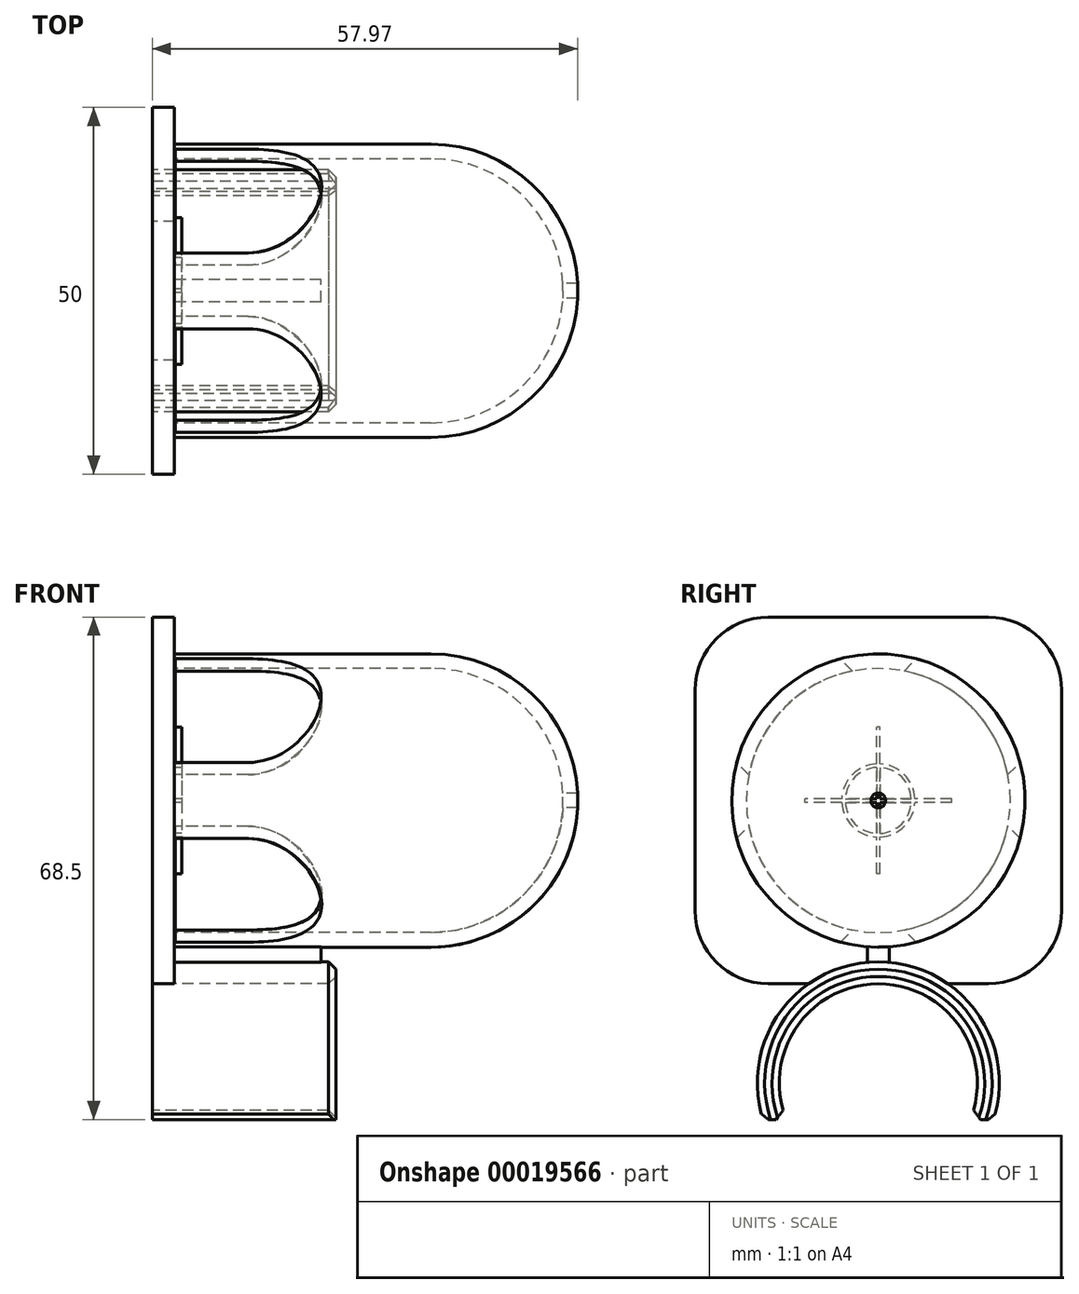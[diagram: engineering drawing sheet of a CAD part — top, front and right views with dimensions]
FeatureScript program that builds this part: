
annotation { "Feature Type Name" : "Feature", "Feature Type Description" : "" }
export const myFeature = defineFeature(function(context is Context, id is Id, definition is map)
    precondition{}
    {
        {
            var Q0;
            Q0=qCreatedBy(makeId("Right.planeOp"),FACE);
            var sketch = newSketch(context, id + "F0", { "sketchPlane" : qUnion([Q0])});
            skCircle(sketch, "E0", {"center": v(0, 0) * mm, "radius": 16.5 * mm});
            skCircle(sketch, "E1", {"center": v(0, 0) * mm, "radius": 13.5 * mm});
            skLineSegment(sketch, "E2", {"start": v(0, 16.5) * mm, "end": v(38.85, 16.5) * mm, "construction": true});
            skSolve(sketch);
        }
        {
            var Q0;
            Q0=qSketchRegion(id+"F0",true);
            extrude(context, id + "F1", {"entities" : qUnion([Q0]), "depth" : 25 * mm});
        }
        {
            var Q0;
            Q0=qCreatedBy(makeId("Right.planeOp"),FACE);
            var sketch = newSketch(context, id + "F23", { "sketchPlane" : qUnion([Q0])});
            skLineSegment(sketch, "E3.bottom", {"start": v(-20, -5) * mm, "end": v(20, -5) * mm});
            skLineSegment(sketch, "E3.top", {"start": v(-20, -25) * mm, "end": v(20, -25) * mm});
            skLineSegment(sketch, "E3.left", {"start": v(-20, -5) * mm, "end": v(-20, -25) * mm});
            skLineSegment(sketch, "E3.right", {"start": v(20, -5) * mm, "end": v(20, -25) * mm});
            skSolve(sketch);
        }
        {
            var Q0;
            Q0=qSketchRegion(id+"F23",true);
            extrude(context, id + "F2", {"entities" : qUnion([Q0]), "operationType" : NewBodyOperationType.REMOVE, "endBound" : BoundingType.SYMMETRIC, "oppositeDirection" : true, "depth" : 50 * mm});
        }
        {
            var Q0;
            Q0=makeQuery(id+"F2.boolean.opBoolean","INTERSECT",EDGE,{"disambiguationData":[OD(1.0)],"derivedFrom":[makeQuery(id+"F1.opExtrude","SWEPT_FACE",FACE,{"disambiguationData":[OSD([sQuery(id+"F0.wireOp",EDGE,"E1")])]}),makeQuery(id+"F2.opExtrude","SWEPT_FACE",FACE,{"disambiguationData":[OSD([sQuery(id+"F23.wireOp",EDGE,"E3.bottom")])]})]});
            var Q1;
            Q1=makeQuery(id+"F2.boolean.opBoolean","INTERSECT",EDGE,{"disambiguationData":[OD(0.0)],"derivedFrom":[makeQuery(id+"F1.opExtrude","SWEPT_FACE",FACE,{"disambiguationData":[OSD([sQuery(id+"F0.wireOp",EDGE,"E1")])]}),makeQuery(id+"F2.opExtrude","SWEPT_FACE",FACE,{"disambiguationData":[OSD([sQuery(id+"F23.wireOp",EDGE,"E3.bottom")])]})]});
            var Q2;
            Q2=makeQuery(id+"F1.opExtrude","CAP_EDGE",EDGE,{"disambiguationData":[OSD([sQuery(id+"F0.wireOp",EDGE,"E1")])],"isStart":false});
            var Q3;
            Q3=makeQuery(id+"F2.boolean.opBoolean","COPY",EDGE,{"disambiguationData":[OD(0.0)],"derivedFrom":makeQuery(id+"F2.opExtrude","CAP_EDGE",EDGE,{"disambiguationData":[OSD([sQuery(id+"F23.wireOp",EDGE,"E3.bottom")])],"isStart":true})});
            var Q4;
            Q4=makeQuery(id+"F2.boolean.opBoolean","INTERSECT",EDGE,{"disambiguationData":[OD(0.0)],"derivedFrom":[makeQuery(id+"F1.opExtrude","SWEPT_FACE",FACE,{"disambiguationData":[OSD([sQuery(id+"F0.wireOp",EDGE,"E0")])]}),makeQuery(id+"F2.opExtrude","SWEPT_FACE",FACE,{"disambiguationData":[OSD([sQuery(id+"F23.wireOp",EDGE,"E3.bottom")])]})]});
            var Q5;
            Q5=makeQuery(id+"F2.boolean.opBoolean","INTERSECT",EDGE,{"disambiguationData":[OD(1.0)],"derivedFrom":[makeQuery(id+"F1.opExtrude","SWEPT_FACE",FACE,{"disambiguationData":[OSD([sQuery(id+"F0.wireOp",EDGE,"E0")])]}),makeQuery(id+"F2.opExtrude","SWEPT_FACE",FACE,{"disambiguationData":[OSD([sQuery(id+"F23.wireOp",EDGE,"E3.bottom")])]})]});
            var Q6;
            Q6=makeQuery(id+"F1.opExtrude","CAP_EDGE",EDGE,{"disambiguationData":[OSD([sQuery(id+"F0.wireOp",EDGE,"E0")])],"isStart":false});
            var Q7;
            Q7=makeQuery(id+"F2.boolean.opBoolean","COPY",EDGE,{"disambiguationData":[OD(1.0)],"derivedFrom":makeQuery(id+"F2.opExtrude","CAP_EDGE",EDGE,{"disambiguationData":[OSD([sQuery(id+"F23.wireOp",EDGE,"E3.bottom")])],"isStart":true})});
            chamfer(context, id + "F24", {"entities" : qUnion([Q0, Q1, Q2, Q3, Q4, Q5, Q6, Q7]), "width" : 1 * mm, "tangentPropagation" : true});
        }
        {
            var Q0;
            Q0=qCreatedBy(makeId("Right.planeOp"),FACE);
            var sketch = newSketch(context, id + "F3", { "sketchPlane" : qUnion([Q0])});
            skLineSegment(sketch, "E4.bottom", {"start": v(-15, 63.5) * mm, "end": v(15, 63.5) * mm});
            skLineSegment(sketch, "E4.top", {"start": v(-15, 13.5) * mm, "end": v(15, 13.5) * mm});
            skLineSegment(sketch, "E4.left", {"start": v(-25, 53.5) * mm, "end": v(-25, 23.5) * mm});
            skLineSegment(sketch, "E4.right", {"start": v(25, 53.5) * mm, "end": v(25, 23.5) * mm});
            skLineSegment(sketch, "E5", {"start": v(-47.36, 38.5) * mm, "end": v(44, 38.5) * mm, "construction": true});
            skLineSegment(sketch, "E6", {"start": v(0, 0) * mm, "end": v(0, 73) * mm, "construction": true});
            skPoint(sketch, "E7.visualSharp", {"position": v(-25, 63.5) * mm});
            skArc(sketch, "E7.filletArc", {"start": v(-15, 63.5) * mm, "mid": v(-22.07, 60.57) * mm, "end": v(-25, 53.5) * mm});
            skPoint(sketch, "E8.visualSharp", {"position": v(25, 63.5) * mm});
            skArc(sketch, "E8.filletArc", {"start": v(25, 53.5) * mm, "mid": v(22.07, 60.57) * mm, "end": v(15, 63.5) * mm});
            skPoint(sketch, "E9.visualSharp", {"position": v(25, 13.5) * mm});
            skArc(sketch, "E9.filletArc", {"start": v(15, 13.5) * mm, "mid": v(22.07, 16.43) * mm, "end": v(25, 23.5) * mm});
            skPoint(sketch, "E10.visualSharp", {"position": v(-25, 13.5) * mm});
            skArc(sketch, "E10.filletArc", {"start": v(-25, 23.5) * mm, "mid": v(-22.07, 16.43) * mm, "end": v(-15, 13.5) * mm});
            skSolve(sketch);
        }
        {
            var Q0;
            Q0=qSketchRegion(id+"F3",true);
            extrude(context, id + "F4", {"entities" : qUnion([Q0]), "operationType" : NewBodyOperationType.ADD, "depth" : 3 * mm});
        }
        {
            var Q0;
            Q0=makeQuery(id+"F4.opExtrude","CAP_FACE",FACE,{"disambiguationData":[OSD([sQuery(id+"F3.wireOp",EDGE,"E4.bottom"),sQuery(id+"F3.wireOp",EDGE,"E4.top"),sQuery(id+"F3.wireOp",EDGE,"E4.left"),sQuery(id+"F3.wireOp",EDGE,"E4.right")])],"isStart":false});
            var sketch = newSketch(context, id + "F5", { "sketchPlane" : qUnion([Q0])});
            skCircle(sketch, "E11", {"center": v(0, 38.5) * mm, "radius": 20 * mm});
            skCircle(sketch, "E12", {"center": v(0, 38.5) * mm, "radius": 18 * mm});
            skSolve(sketch);
        }
        {
            var Q0;
            Q0 = qSketchRegion(id + "F5", true);
            extrude(context, id + "F6", {"entities" : qUnion([Q0]), "operationType" : NewBodyOperationType.ADD, "depth" : 35 * mm});
        }
        {
            var Q0;
            Q0=qCreatedBy(makeId("Top.planeOp"),FACE);
            cPlane(context, id + "F7", {"entities" : qUnion([Q0]), "cplaneType" : CPlaneType.OFFSET, "offset" : 38.5 * mm, "width" : 150 * mm, "height" : 150 * mm});
        }
        {
            var Q0;
            Q0=qCreatedBy(id+"F7.planeOp",FACE);
            var sketch = newSketch(context, id + "F8", { "sketchPlane" : qUnion([Q0])});
            skLineSegment(sketch, "E13", {"start": v(0, 0) * mm, "end": v(132.1, 0) * mm, "construction": true});
            skSolve(sketch);
        }
        {
            var Q0;
            Q0=sQuery(id+"F8.wireOp",EDGE,"E13");
            cPlane(context, id + "F9", {"entities" : qUnion([Q0]), "cplaneType" : CPlaneType.LINE_ANGLE, "offset" : 150 * mm, "angle" : 45 * degree, "width" : 150 * mm, "height" : 150 * mm});
        }
        {
            var Q0;
            Q0=sQuery(id+"F8.wireOp",EDGE,"E13");
            cPlane(context, id + "F10", {"entities" : qUnion([Q0]), "cplaneType" : CPlaneType.LINE_ANGLE, "offset" : 150 * mm, "angle" : 135 * degree, "width" : 150 * mm, "height" : 150 * mm});
        }
        {
            var Q0;
            Q0=qCreatedBy(id+"F9.planeOp",FACE);
            var sketch = newSketch(context, id + "F11", { "sketchPlane" : qUnion([Q0])});
            skLineSegment(sketch, "E14.bottom", {"start": v(-13.1, 37.22) * mm, "end": v(-3.1, 37.22) * mm});
            skLineSegment(sketch, "E14.top", {"start": v(-13.1, 17.22) * mm, "end": v(-3.1, 17.22) * mm});
            skLineSegment(sketch, "E14.right", {"start": v(-3.1, 37.22) * mm, "end": v(-3.1, 17.22) * mm});
            skArc(sketch, "E15", {"start": v(-13.1, 37.22) * mm, "mid": v(-23.1, 27.22) * mm, "end": v(-13.1, 17.22) * mm});
            skSolve(sketch);
        }
        {
            var Q0;
            Q0 = qSketchRegion(id + "F11", true);
            extrude(context, id + "F12", {"entities" : qUnion([Q0]), "operationType" : NewBodyOperationType.REMOVE, "endBound" : BoundingType.SYMMETRIC, "oppositeDirection" : true, "depth" : 40 * mm});
        }
        {
            var Q0;
            Q0=qCreatedBy(id+"F10.planeOp",FACE);
            var sketch = newSketch(context, id + "F13", { "sketchPlane" : qUnion([Q0])});
            skLineSegment(sketch, "E16.bottom", {"start": v(3.1, 37.22) * mm, "end": v(13, 37.22) * mm});
            skLineSegment(sketch, "E16.top", {"start": v(3.1, 17.22) * mm, "end": v(13, 17.22) * mm});
            skLineSegment(sketch, "E16.left", {"start": v(3.1, 37.22) * mm, "end": v(3.1, 17.22) * mm});
            skArc(sketch, "E17", {"start": v(13, 17.22) * mm, "mid": v(23, 27.22) * mm, "end": v(13, 37.22) * mm});
            skSolve(sketch);
        }
        {
            var Q0;
            Q0 = qSketchRegion(id + "F13", true);
            extrude(context, id + "F14", {"entities" : qUnion([Q0]), "operationType" : NewBodyOperationType.REMOVE, "endBound" : BoundingType.SYMMETRIC, "oppositeDirection" : true, "depth" : 42.5 * mm});
        }
        {
            var Q0;
            Q0=qCreatedBy(makeId("Front.planeOp"),FACE);
            var sketch = newSketch(context, id + "F15", { "sketchPlane" : qUnion([Q0])});
            skLineSegment(sketch, "E18", {"start": v(0, 38.5) * mm, "end": v(115.15, 38.5) * mm, "construction": true});
            skArc(sketch, "E19", {"start": v(38, 18.5) * mm, "mid": v(52.14, 24.36) * mm, "end": v(58, 38.5) * mm});
            skArc(sketch, "E20", {"start": v(37.99, 20.5) * mm, "mid": v(50.72, 25.77) * mm, "end": v(56, 38.5) * mm});
            skLineSegment(sketch, "E21", {"start": v(37.99, 20.5) * mm, "end": v(38, 18.5) * mm});
            skLineSegment(sketch, "E22", {"start": v(56, 38.5) * mm, "end": v(58, 38.5) * mm});
            skSolve(sketch);
        }
        {
            var Q0;
            Q0 = qSketchRegion(id + "F15", true);
            var Q1;
            Q1=sQuery(id+"F15.wireOp",EDGE,"E18");
            revolve(context, id + "F16", {"operationType" : NewBodyOperationType.ADD, "entities" : qUnion([Q0]), "axis" : qUnion([Q1]), "revolveType" : RevolveType.FULL});
        }
        {
            var Q0;
            Q0=qCreatedBy(makeId("Right.planeOp"),FACE);
            var sketch = newSketch(context, id + "F17", { "sketchPlane" : qUnion([Q0])});
            skArc(sketch, "E23", {"start": v(-0.25, 43) * mm, "mid": v(-3.18, 41.68) * mm, "end": v(-4.5, 38.75) * mm});
            skArc(sketch, "E24", {"start": v(-0.25, 43.5) * mm, "mid": v(-3.54, 42.04) * mm, "end": v(-5, 38.75) * mm});
            skLineSegment(sketch, "E25.bottom", {"start": v(-10, 38.75) * mm, "end": v(-5, 38.75) * mm});
            skLineSegment(sketch, "E25.top", {"start": v(-10, 38.25) * mm, "end": v(-5, 38.25) * mm});
            skLineSegment(sketch, "E25.left", {"start": v(-10, 38.75) * mm, "end": v(-10, 38.25) * mm});
            skLineSegment(sketch, "E25.right", {"start": v(10, 38.75) * mm, "end": v(10, 38.25) * mm});
            skLineSegment(sketch, "E26.bottom", {"start": v(-0.25, 48.5) * mm, "end": v(0.25, 48.5) * mm});
            skLineSegment(sketch, "E26.top", {"start": v(-0.25, 28.5) * mm, "end": v(0.25, 28.5) * mm});
            skLineSegment(sketch, "E26.left", {"start": v(-0.25, 48.5) * mm, "end": v(-0.25, 43.5) * mm});
            skLineSegment(sketch, "E26.right", {"start": v(0.25, 48.5) * mm, "end": v(0.25, 43.5) * mm});
            skLineSegment(sketch, "E27.trimOffspring", {"start": v(-0.25, 43) * mm, "end": v(-0.25, 38.75) * mm});
            skLineSegment(sketch, "E28.trimOffspring", {"start": v(0.25, 43) * mm, "end": v(0.25, 38.75) * mm});
            skArc(sketch, "E29.trimOffspring", {"start": v(5, 38.75) * mm, "mid": v(3.54, 42.04) * mm, "end": v(0.25, 43.5) * mm});
            skArc(sketch, "E30.trimOffspring", {"start": v(4.5, 38.75) * mm, "mid": v(3.18, 41.68) * mm, "end": v(0.25, 43) * mm});
            skLineSegment(sketch, "E31.trimOffspring", {"start": v(5, 38.75) * mm, "end": v(10, 38.75) * mm});
            skLineSegment(sketch, "E32.trimOffspring", {"start": v(5, 38.25) * mm, "end": v(10, 38.25) * mm});
            skLineSegment(sketch, "E33.trimOffspring", {"start": v(0.25, 38.75) * mm, "end": v(4.5, 38.75) * mm});
            skLineSegment(sketch, "E34.trimOffspring", {"start": v(-0.25, 38.25) * mm, "end": v(-0.25, 34) * mm});
            skLineSegment(sketch, "E35.trimOffspring", {"start": v(0.25, 38.25) * mm, "end": v(4.5, 38.25) * mm});
            skLineSegment(sketch, "E36.trimOffspring", {"start": v(0.25, 38.25) * mm, "end": v(0.25, 34) * mm});
            skArc(sketch, "E37.trimOffspring", {"start": v(0.25, 34) * mm, "mid": v(3.18, 35.32) * mm, "end": v(4.5, 38.25) * mm});
            skArc(sketch, "E38.trimOffspring", {"start": v(0.25, 33.5) * mm, "mid": v(3.54, 34.96) * mm, "end": v(5, 38.25) * mm});
            skLineSegment(sketch, "E39.trimOffspring", {"start": v(-0.25, 33.5) * mm, "end": v(-0.25, 28.5) * mm});
            skLineSegment(sketch, "E40.trimOffspring", {"start": v(0.25, 33.5) * mm, "end": v(0.25, 28.5) * mm});
            skLineSegment(sketch, "E41.trimOffspring", {"start": v(-4.5, 38.75) * mm, "end": v(-0.25, 38.75) * mm});
            skLineSegment(sketch, "E42.trimOffspring", {"start": v(-4.5, 38.25) * mm, "end": v(-0.25, 38.25) * mm});
            skArc(sketch, "E43.trimOffspring", {"start": v(-5, 38.25) * mm, "mid": v(-3.54, 34.96) * mm, "end": v(-0.25, 33.5) * mm});
            skArc(sketch, "E44.trimOffspring", {"start": v(-4.5, 38.25) * mm, "mid": v(-3.18, 35.32) * mm, "end": v(-0.25, 34) * mm});
            skSolve(sketch);
        }
        {
            var Q0;
            Q0 = qSketchRegion(id + "F17", true);
            extrude(context, id + "F18", {"entities" : qUnion([Q0]), "operationType" : NewBodyOperationType.ADD, "depth" : 4 * mm});
        }
        {
            var Q0;
            Q0=makeQuery(id+"F18.opExtrude","CAP_FACE",FACE,{"disambiguationData":[OSD([sQuery(id+"F17.wireOp",EDGE,"E23"),sQuery(id+"F17.wireOp",EDGE,"E24"),sQuery(id+"F17.wireOp",EDGE,"E25.bottom"),sQuery(id+"F17.wireOp",EDGE,"E25.top"),sQuery(id+"F17.wireOp",EDGE,"E25.left"),sQuery(id+"F17.wireOp",EDGE,"E25.right"),sQuery(id+"F17.wireOp",EDGE,"E26.bottom"),sQuery(id+"F17.wireOp",EDGE,"E26.top"),sQuery(id+"F17.wireOp",EDGE,"E26.left"),sQuery(id+"F17.wireOp",EDGE,"E26.right"),sQuery(id+"F17.wireOp",EDGE,"E27.trimOffspring"),sQuery(id+"F17.wireOp",EDGE,"E28.trimOffspring"),sQuery(id+"F17.wireOp",EDGE,"E29.trimOffspring"),sQuery(id+"F17.wireOp",EDGE,"E30.trimOffspring"),sQuery(id+"F17.wireOp",EDGE,"E31.trimOffspring"),sQuery(id+"F17.wireOp",EDGE,"E32.trimOffspring"),sQuery(id+"F17.wireOp",EDGE,"E33.trimOffspring"),sQuery(id+"F17.wireOp",EDGE,"E34.trimOffspring"),sQuery(id+"F17.wireOp",EDGE,"E35.trimOffspring"),sQuery(id+"F17.wireOp",EDGE,"E36.trimOffspring"),sQuery(id+"F17.wireOp",EDGE,"E37.trimOffspring"),sQuery(id+"F17.wireOp",EDGE,"E38.trimOffspring"),sQuery(id+"F17.wireOp",EDGE,"E39.trimOffspring"),sQuery(id+"F17.wireOp",EDGE,"E40.trimOffspring"),sQuery(id+"F17.wireOp",EDGE,"E41.trimOffspring"),sQuery(id+"F17.wireOp",EDGE,"E42.trimOffspring"),sQuery(id+"F17.wireOp",EDGE,"E43.trimOffspring"),sQuery(id+"F17.wireOp",EDGE,"E44.trimOffspring")])],"isStart":false});
            var sketch = newSketch(context, id + "F19", { "sketchPlane" : qUnion([Q0])});
            skCircle(sketch, "E45", {"center": v(0, 38.5) * mm, "radius": 1 * mm});
            skSolve(sketch);
        }
        {
            var Q0;
            Q0 = qSketchRegion(id + "F19", true);
            extrude(context, id + "F20", {"entities" : qUnion([Q0]), "operationType" : NewBodyOperationType.REMOVE, "depth" : 200 * mm});
        }
        {
            var Q0;
            {var subQ0=sQuery(id+"F3.wireOp",EDGE,"E4.bottom");var subQ1=sQuery(id+"F3.wireOp",EDGE,"E4.top");var subQ2=sQuery(id+"F3.wireOp",EDGE,"E4.left");var subQ3=sQuery(id+"F3.wireOp",EDGE,"E4.right");Q0=makeQuery(id+"F6.boolean.opBoolean","SPLIT",FACE,{"disambiguationData":[TD([makeQuery(id+"F1.opExtrude","SWEPT_FACE",FACE,{"disambiguationData":[OSD([sQuery(id+"F0.wireOp",EDGE,"E0")])]})])],"derivedFrom":makeQuery(id+"F4.opExtrude","CAP_FACE",FACE,{"disambiguationData":[OSD([subQ0,subQ1,subQ2,subQ3])],"isStart":false})});}
            var sketch = newSketch(context, id + "F21", { "sketchPlane" : qUnion([Q0])});
            skLineSegment(sketch, "E46.bottom", {"start": v(-1.5, 19.5) * mm, "end": v(1.5, 19.5) * mm});
            skLineSegment(sketch, "E46.top", {"start": v(-1.5, 14.5) * mm, "end": v(1.5, 14.5) * mm});
            skLineSegment(sketch, "E46.left", {"start": v(-1.5, 19.5) * mm, "end": v(-1.5, 14.5) * mm});
            skLineSegment(sketch, "E46.right", {"start": v(1.5, 19.5) * mm, "end": v(1.5, 14.5) * mm});
            skSolve(sketch);
        }
        {
            var Q0;
            Q0 = qSketchRegion(id + "F21", true);
            extrude(context, id + "F22", {"entities" : qUnion([Q0]), "operationType" : NewBodyOperationType.ADD, "depth" : 20 * mm});
        }
    });
